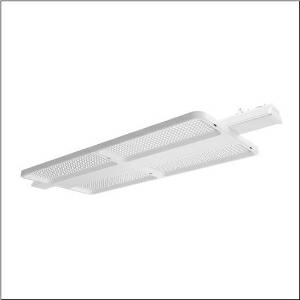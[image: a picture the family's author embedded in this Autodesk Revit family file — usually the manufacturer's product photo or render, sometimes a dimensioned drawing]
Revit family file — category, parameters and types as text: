
# Revit family: highbay_21_fur_licross_r__tragschiene_maxi_52hn11db4mla02_6ba4
name_source: partatom
category: Lighting Fixtures
units: mm (PartAtom-declared; Revit-internal decimal feet)

## family parameters
Cut with Voids When Loaded = No
Host = Face
Light Source = No
Part Type = Normal
Room Calculation Point = No
Round Connector Dimension = Use Diameter
Shared = No

## types (1)
- --- (1 x LED, 28000 lm, 144.5 W, 4000K)
    Apparent Load = 144 VA
    CIE Flux Codes = 89 97 99 100 100
    Color Rendering = 80
    Color Temperature = 4000K
    Default Elevation = 1800 mm
    Description = high bay luminaire Highbay 21 for Licross® trunking rail maxi; direct symmetric narrow distribution, light control with lens of PMMA; UGR ≤ 19 (X = 4H | Y = 8H | S = 0.25H | reflection values 70/50/20); luminous flux: 28.000lm; light colour: 840, colour temperature: 4000K, MacAdam ≤ 3 SDCM (initial), colour rendering: CRI > 80; luminous efficacy: 193,8lm/W; rated service life: 75.000h (L80/B50) at AT= ta max; control: Bluetooth® Mesh; for wireless networking: Node luminaire for setting up a local control solution without a higher-level application controller, intelligence completely in the luminaire; no control line such as DALI between the Node multi-sensor luminaires and Nodes is required, wireless integration of other Node luminaires and Node multi-sensor luminaires into the network is possible; number of Node luminaires in the project can be expanded as required, network sizes > 300 Nodes can be realized; can also be connected to lighting or building automation via various gateways upon request; integrated DALI2 ECG provides luminaire data (according to IEC62386, Part 251), energy data (Part 252), and monitoring and analytics data (Part 253) to higher-level systems for further processing; luminaire connection: plug, 5-pole, with phase selectionmains connection: 230..240V, AC 50/60Hz; connected load: 144,5W; protection rating (complete): IP64; insulation class (complete): insulation class I (protective earthing); protection symbol: D; impact resistance: IK08; certification: CE, ENEC, VDE, UKCA; internal wiring halogen-free; luminaire LABS conformity tested according to VDMA 24364:2018-05; corresponds to IFS (International Featured Standards) requirements for safety and quality in the food industry; housing frame of high-performance plastic PA6, matt traffic white (RAL 9016); cover of PMMA; fixing on rail side of steel, galvanised, white; blank cover of PC/ABS, traffic white (RAL 9016); dimension (LxWxH): 1.250 x 442 x 71mm; permissible operating ambient temperature: -20..+45°C (reducing of maximum allowable ambient temperature of 5°C with ceiling mounting); packaging unit: 1 piece
    Height = 72 mm  [stored 0.23622 ft]
    Lamp = 1 x LED
    Lamp Light Flux = 28000 lm
    Lamp Power = 144.5 W
    Lamp count = 1
    Length = 946 mm
    Luminous efficacy = 194 lm/W
    Manufacturer = Siteco
    ModVariant = No
    Model = 52HN11DB4MLA02
    Mounting Place = Ceiling
    Mounting Type = Pendant
    Number of Poles = 1
    OnlyDefault = Yes
    Power Factor = 1
    Product Name = Highbay 21 für Licross® Tragschiene maxi
    Product group = high bay luminaire
    ProductGroupID = 901
    Protection Class = Protection class I
    Protection Degree = IP 64
    RLX_Detail_Level = 1
    RLX_Emergency_Light_Flux = 0 lm
    RLX_Emergency_Type = 0
    RLX_Emergency_Type_DB = No
    RlxData = <blob elided: 131217 chars, md5=2f0464ce>
    Socket = socket
    Standby Power = 0 W
    System Light Flux = 28000 lm
    System Power = 144 W
    Type Comments = factory setting: luminous flux: 100 % | dim-lin: 254 | 668 mA
    Type Image = l_1361711.jpg
    URL = http://relux.com
    VarID = @adj_009561
    Voltage = 0 V
    Weight = 0.00 kg
    Width = 442 mm

note: [stored X ft] marks values corroborated as IEEE doubles in the binary element streams (Revit-internal decimal feet)

## geometry (parser evidence)
native form markers: Blend x4, Sweep x11
no freeform markers — native parametric forms only
